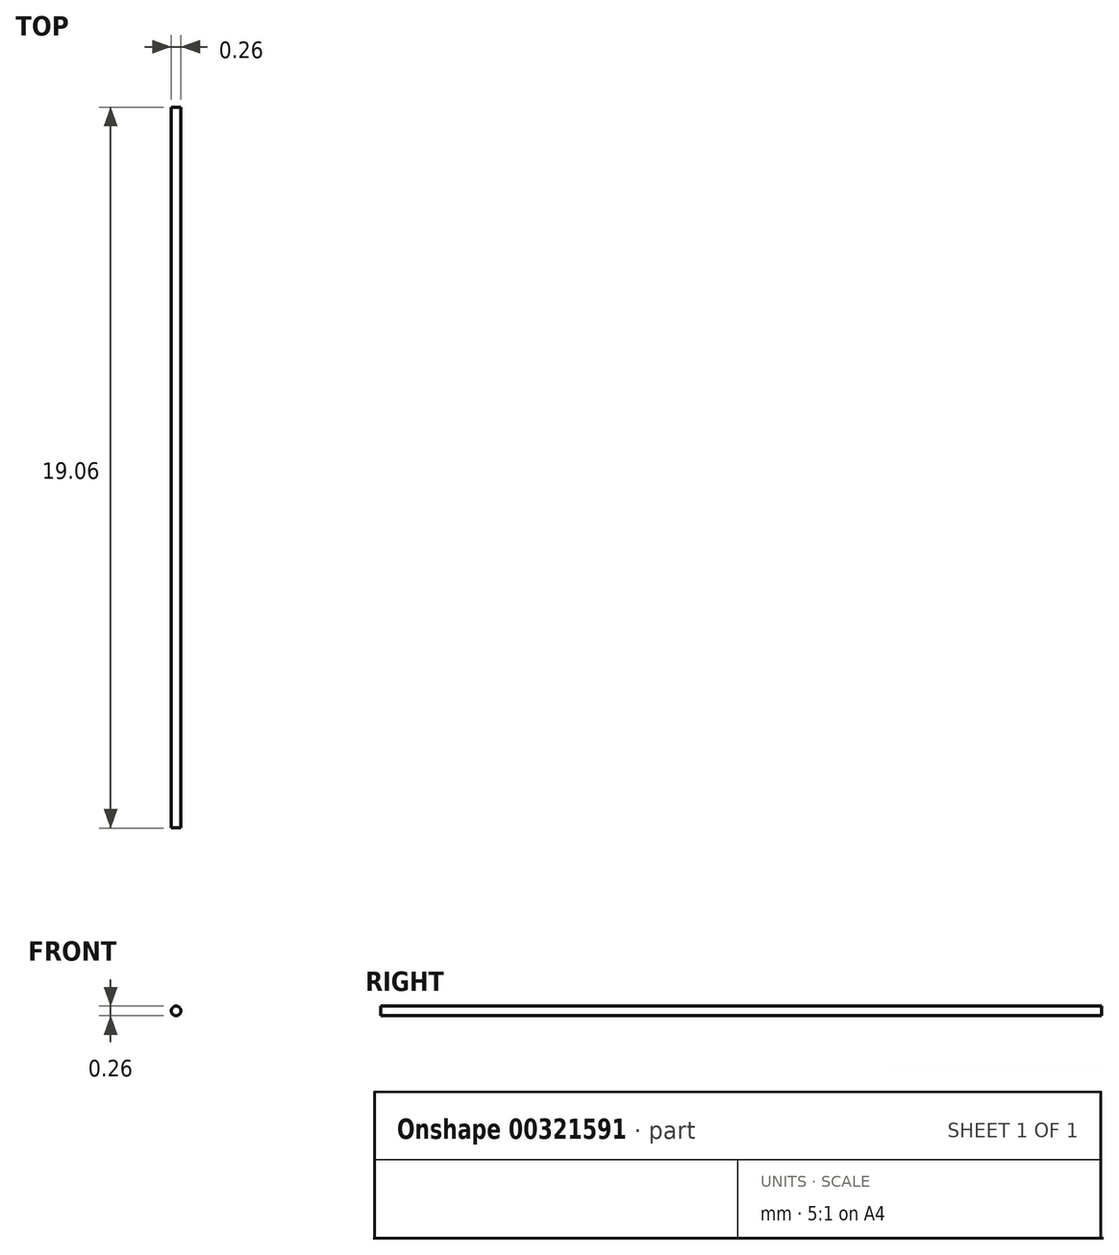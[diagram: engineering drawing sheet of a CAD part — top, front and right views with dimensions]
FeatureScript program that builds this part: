
annotation { "Feature Type Name" : "Feature", "Feature Type Description" : "" }
export const myFeature = defineFeature(function(context is Context, id is Id, definition is map)
    precondition{}
    {
        {
            var Q0;
            Q0=qCreatedBy(makeId("Front.planeOp"),FACE);
            var sketch = newSketch(context, id + "F0", { "sketchPlane" : qUnion([Q0])});
            skCircle(sketch, "E0", {"center": v(0, 0) * mm, "radius": 0.38 * mm});
            skLineSegment(sketch, "E1", {"start": v(0, 0) * mm, "end": v(0, 4.5) * mm, "construction": true});
            skCircle(sketch, "E2", {"center": v(0, 2.5) * mm, "radius": 0.63 * mm});
            skCircle(sketch, "E3", {"center": v(0, 4.5) * mm, "radius": 0.38 * mm});
            skLineSegment(sketch, "E4", {"start": v(0, 0) * mm, "end": v(1.75, 0) * mm, "construction": true});
            skCircle(sketch, "E5", {"center": v(1.75, 0) * mm, "radius": 0.31 * mm});
            skLineSegment(sketch, "E6", {"start": v(-0.37, 4.55) * mm, "end": v(-0.62, 2.58) * mm});
            skLineSegment(sketch, "E7", {"start": v(0.37, 4.55) * mm, "end": v(0.62, 2.58) * mm});
            skLineSegment(sketch, "E8", {"start": v(-0.62, 2.44) * mm, "end": v(-0.37, -0.04) * mm});
            skLineSegment(sketch, "E9", {"start": v(0.62, 2.44) * mm, "end": v(0.45, 0.7) * mm});
            skLineSegment(sketch, "E10", {"start": v(0, 0.37) * mm, "end": v(0.03, 0.37) * mm});
            skLineSegment(sketch, "E11", {"start": v(0, -0.37) * mm, "end": v(1.76, -0.31) * mm});
            skCircle(sketch, "E12", {"center": v(0, 4.5) * mm, "radius": 0.12 * mm});
            skCircle(sketch, "E13", {"center": v(0, 2.5) * mm, "radius": 0.12 * mm});
            skCircle(sketch, "E14", {"center": v(0, 0) * mm, "radius": 0.12 * mm});
            skCircle(sketch, "E15", {"center": v(1.75, 0) * mm, "radius": 0.12 * mm});
            skLineSegment(sketch, "E16.trimOffspring", {"start": v(0.75, 0.35) * mm, "end": v(1.76, 0.31) * mm});
            skLineSegment(sketch, "E17.trimOffspring", {"start": v(0.38, 0) * mm, "end": v(0.37, -0.04) * mm});
            skPoint(sketch, "E18.visualSharp", {"position": v(0.41, 0.36) * mm});
            skArc(sketch, "E18.filletArc", {"start": v(0.45, 0.7) * mm, "mid": v(0.52, 0.46) * mm, "end": v(0.75, 0.35) * mm});
            skCircle(sketch, "E19", {"center": v(-0.06, 3.94) * mm, "radius": 0.12 * mm});
            skSolve(sketch);
        }
        {
            var Q0;
            Q0=sQuery(id+"F0.wireOp",EDGE,"E13");
            extrude(context, id + "F1", {"bodyType" : ToolBodyType.SURFACE, "surfaceEntities" : qUnion([Q0]), "endBound" : BoundingType.SYMMETRIC, "depth" : 19.05 * mm});
        }
    });
